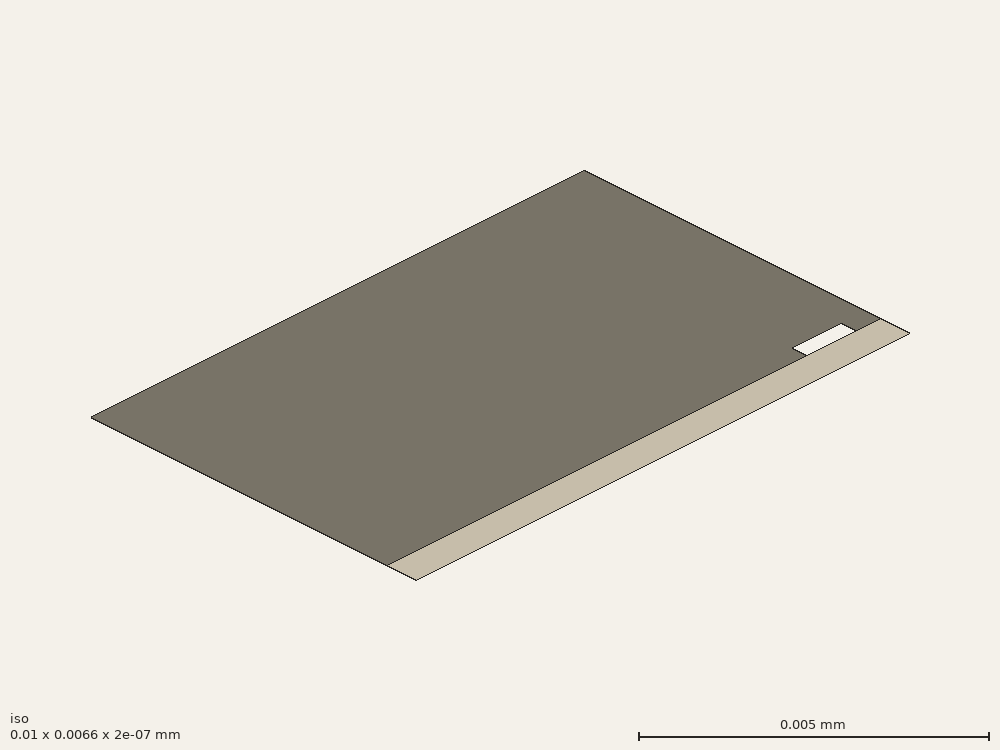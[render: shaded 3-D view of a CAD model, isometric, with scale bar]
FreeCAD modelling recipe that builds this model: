
FCSTD DOCUMENT  (FreeCAD 0.21R33694 (Git))
Label: diffPair
License: All rights reserved
LicenseURL: http://en.wikipedia.org/wiki/All_rights_reserved
objects: Part::Part2DObjectPython×6, App::FeaturePython×3, Part::FeaturePython×2, Part::Cut×1
note: 9 computed .brp shape members not serialized (recipe doc carries the construction recipe); baked Part::Feature solids carry a one-line shape summary decoded from their .brp

FEATURE [Part::Part2DObjectPython] Rectangle  label="substrate"  # Draft 2D object (typed FeaturePython)
  Area = 6.35
  ChamferSize = 0
  Columns = 1
  FilletRadius = 0
  Height = 0.635
  Length = 10
  MakeFace = true
  Placement = pos=(-10,0,0) rot=(0,0,1;0rad)
  Rows = 1
FEATURE [Part::Part2DObjectPython] Wire  label="air"  # Draft 2D object (typed FeaturePython)
  Area = 119.4
  ChamferSize = 0
  Closed = true
  End = (-1.5,0.635,0)
  FilletRadius = 0
  Length = 53.2
  MakeFace = true
  Placement = pos=(-10,0.635,0) rot=(0,0,1;0rad)
  Points = (12) [(0,0,0),(0,6,0),(20,6,0),(20,-6.66134e-16,0),(11.5,-3.33067e-16,0),(11.5,0.3,0),(10.5,0.3,0),(10.5,-3.33067e-16,0),(9.5,-3.33067e-16,0),(9.5,0.3,0),(8.5,0.3,0),(8.5,-3.33067e-16,0)]
  Start = (-10,0.635,0)
  Subdivisions = 0
FEATURE [Part::Part2DObjectPython] Rectangle003  label="_Pline1"  # Draft 2D object (typed FeaturePython)
  Area = 0
  ChamferSize = 0
  Columns = 1
  FilletRadius = 0
  Height = 0.0003
  Length = 0.001
  MakeFace = false
  Placement = pos=(-0.0015,0.000635,0) rot=(0,0,1;0rad)
  Rows = 1
FEATURE [App::FeaturePython] Text  label="_M1(current){line1}"  # WARN: FeaturePython — macro-defined, semantics opaque (R4)
  Placement = pos=(-0.00185272,-0.00154398,0) rot=(0,0,1;0rad)
  Text = .
FEATURE [App::FeaturePython] Text001  label="_M1(voltage){V1}"  # WARN: FeaturePython — macro-defined, semantics opaque (R4)
  Placement = pos=(-0.00185272,-0.00154398,0) rot=(0,0,1;0rad)
  Text = .
FEATURE [Part::Part2DObjectPython] Rectangle004  # Draft 2D object (typed FeaturePython)
  Area = 60
  ChamferSize = 0
  Columns = 1
  FilletRadius = 0
  Height = 6
  Length = 10
  MakeFace = true
  Placement = pos=(0,0.635,0) rot=(0,0,1;0rad)
  Rows = 1
FEATURE [Part::Cut] Cut
  Base = -> Wire
  Tool = -> Rectangle004
FEATURE [Part::FeaturePython] BooleanFragments  # WARN: FeaturePython — macro-defined, semantics opaque (R4)
  Mode = 0
  Objects = -> [Rectangle,Cut]
  Tolerance = 0
FEATURE [Part::FeaturePython] Clone  label="scaled to mm"  # Draft clone (typed FeaturePython)
  AttacherType = Attacher::AttachEngine3D
  Fuse = false
  Objects = -> [BooleanFragments]
  Scale = (0.001,0.001,1)
FEATURE [Part::Part2DObjectPython] Line001  label="_Pline2"  # Draft 2D object (typed FeaturePython)
  Area = 0
  ChamferSize = 0
  Closed = false
  End = (0,0,0)
  FilletRadius = 0
  Length = 0.006635
  MakeFace = true
  Placement = pos=(0,0.006635,0) rot=(0,0,1;0rad)
  Points = (2) [(0,0,0),(-1.94413e-20,-0.006635,0)]
  Start = (0,0.006635,0)
  Subdivisions = 0
FEATURE [App::FeaturePython] Text002  label="_B1(PMC){line2}"  # WARN: FeaturePython — macro-defined, semantics opaque (R4)
  Placement = pos=(-0.00739341,-0.00151859,0) rot=(0,0,1;0rad)
  Text = .
FEATURE [Part::Part2DObjectPython] Line002  label="_PV1"  # Draft 2D object (typed FeaturePython)
  Area = 0
  ChamferSize = 0
  Closed = false
  End = (-0.001,0.000635,0)
  FilletRadius = 0
  Length = 0.000635
  MakeFace = true
  Placement = pos=(-0.001,0,0) rot=(0,1,0;3.14159rad)
  Points = (2) [(0,0,0),(0,0.000635,0)]
  Start = (-0.001,0,0)
  Subdivisions = 0
